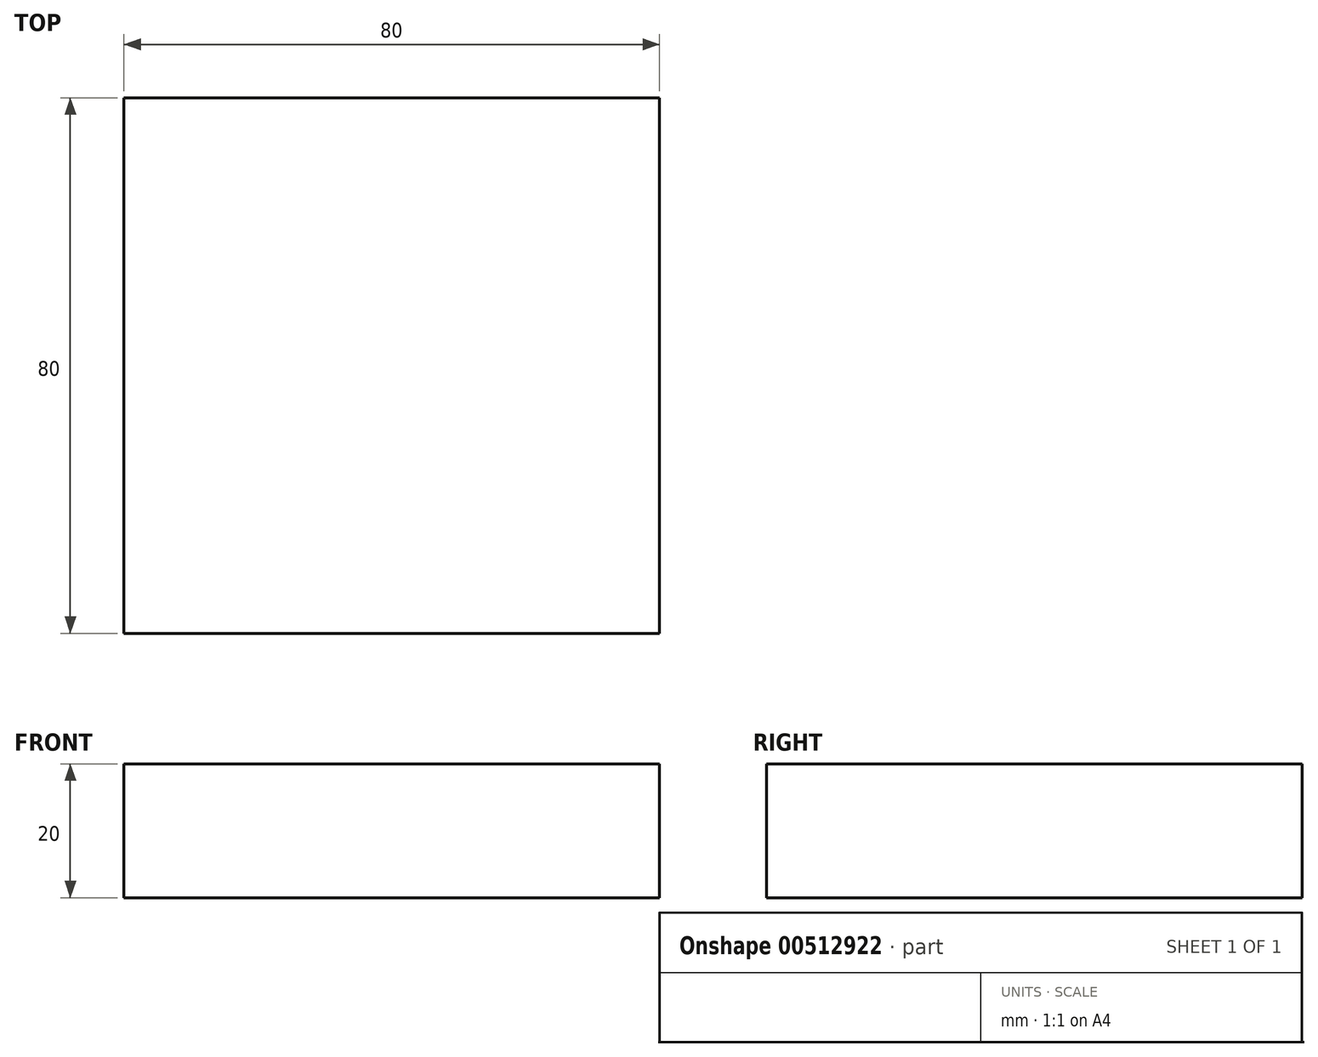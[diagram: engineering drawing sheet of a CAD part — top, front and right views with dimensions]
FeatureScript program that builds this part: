
annotation { "Feature Type Name" : "Feature", "Feature Type Description" : "" }
export const myFeature = defineFeature(function(context is Context, id is Id, definition is map)
    precondition{}
    {
        {
            var Q0;
            Q0=qCreatedBy(makeId("Top.planeOp"),FACE);
            var sketch = newSketch(context, id + "F0", { "sketchPlane" : qUnion([Q0])});
            skLineSegment(sketch, "E0.bottom", {"start": v(40, -40) * mm, "end": v(-40, -40) * mm});
            skLineSegment(sketch, "E0.top", {"start": v(40, 40) * mm, "end": v(-40, 40) * mm});
            skLineSegment(sketch, "E0.left", {"start": v(40, -40) * mm, "end": v(40, 40) * mm});
            skLineSegment(sketch, "E0.right", {"start": v(-40, -40) * mm, "end": v(-40, 40) * mm});
            skPoint(sketch, "E0.middle", {"position": v(0, 0) * mm});
            skSolve(sketch);
        }
        {
            var Q0;
            Q0=makeQuery(id+"F0.imprint","IMPRINT",FACE,{"disambiguationData":[TD([[makeQuery(id+"F0.imprint","IMPRINT",EDGE,{"derivedFrom":sQuery(id+"F0.wireOp",EDGE,"E0.bottom")}),-1.0]])]});
            var Q1;
            Q1=makeQuery(id+"F0.imprint","IMPRINT",FACE,{"disambiguationData":[TD([[makeQuery(id+"F0.imprint","IMPRINT",EDGE,{"derivedFrom":sQuery(id+"F0.wireOp",EDGE,"990abf9f-4fc8-4d14-a5ce-889d00fade7d.0")}),1.0]])]});
            extrude(context, id + "F1", {"entities" : qUnion([Q0, Q1]), "oppositeDirection" : true, "depth" : 20 * mm});
        }
    });
